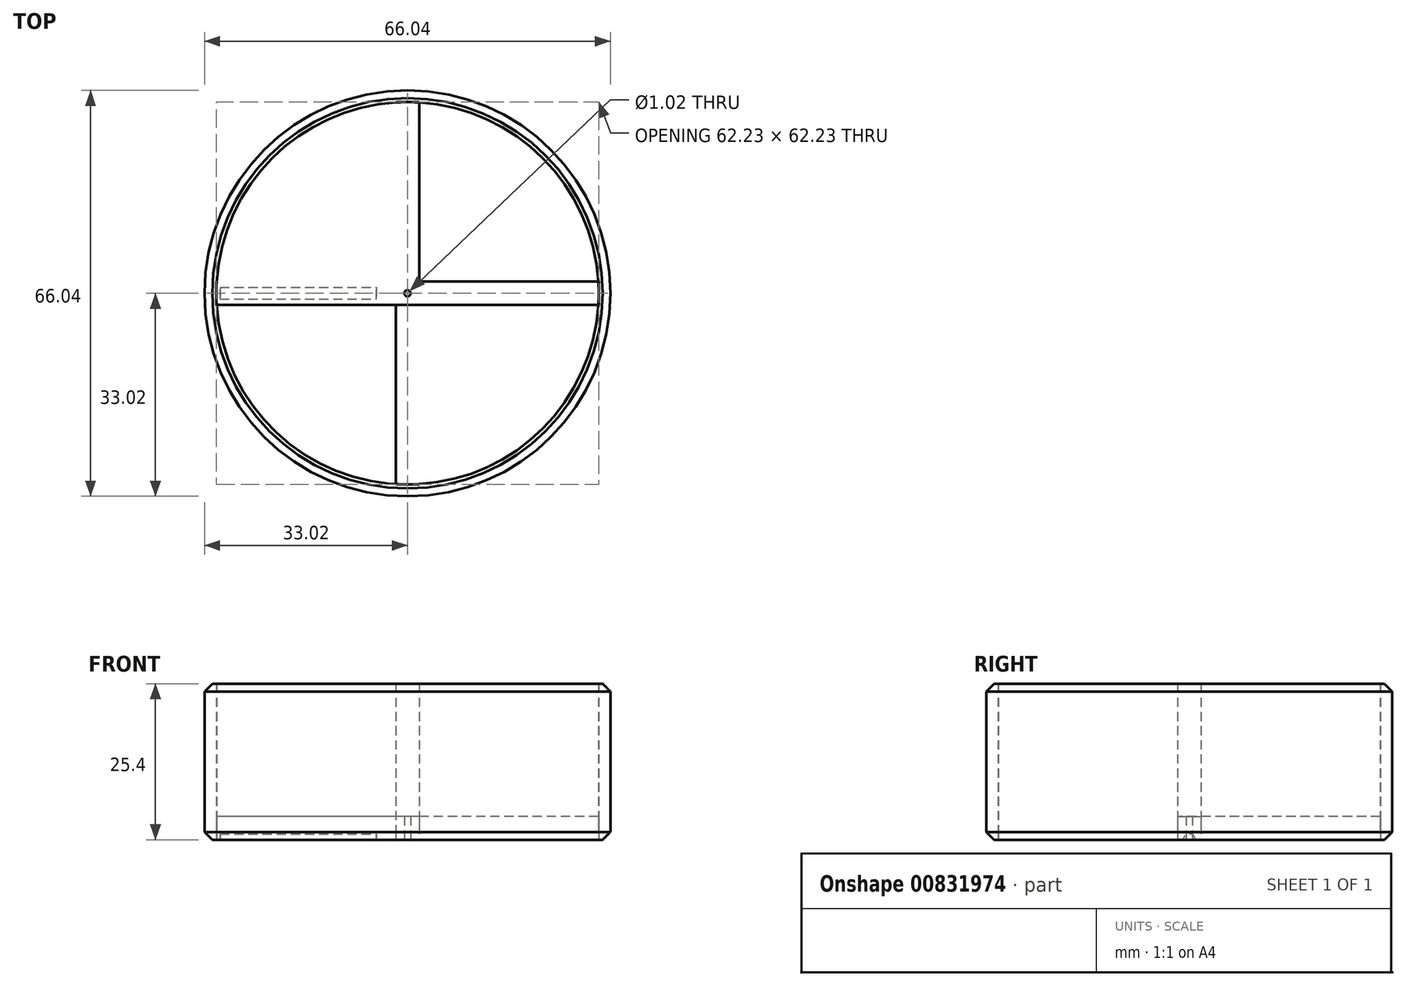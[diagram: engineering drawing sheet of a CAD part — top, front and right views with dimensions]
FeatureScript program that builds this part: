
annotation { "Feature Type Name" : "Feature", "Feature Type Description" : "" }
export const myFeature = defineFeature(function(context is Context, id is Id, definition is map)
    precondition{}
    {
        {
            var Q0;
            Q0=qCreatedBy(makeId("Top.planeOp"),FACE);
            var sketch = newSketch(context, id + "F0", { "sketchPlane" : qUnion([Q0])});
            skCircle(sketch, "E0", {"center": v(0, 0) * mm, "radius": 33.02 * mm});
            skCircle(sketch, "E1", {"center": v(0, 0) * mm, "radius": 31.12 * mm});
            skLineSegment(sketch, "E2.bottom", {"start": v(1.9, 31.12) * mm, "end": v(-1.9, 31.12) * mm});
            skLineSegment(sketch, "E2.top", {"start": v(1.9, -31.12) * mm, "end": v(-1.9, -31.12) * mm});
            skLineSegment(sketch, "E2.left", {"start": v(1.9, 31.12) * mm, "end": v(1.9, -31.12) * mm});
            skLineSegment(sketch, "E2.right", {"start": v(-1.9, 31.12) * mm, "end": v(-1.9, -31.06) * mm});
            skLineSegment(sketch, "E3.bottom", {"start": v(31.12, 1.9) * mm, "end": v(-31.12, 1.9) * mm});
            skLineSegment(sketch, "E3.top", {"start": v(31.12, -1.9) * mm, "end": v(-31.12, -1.9) * mm});
            skLineSegment(sketch, "E3.left", {"start": v(31.12, 1.9) * mm, "end": v(31.12, -1.9) * mm});
            skLineSegment(sketch, "E3.right", {"start": v(-31.12, 1.9) * mm, "end": v(-31.12, -1.9) * mm});
            skCircle(sketch, "E4", {"center": v(0, 0) * mm, "radius": 0.5 * mm});
            skSolve(sketch);
        }
        {
            var Q0;
            {var subQ0=sQuery(id+"F0.wireOp",EDGE,"E2.left");var subQ1=sQuery(id+"F0.wireOp",EDGE,"ze4YUoH1-U5XD-7e5n-4wEU-s4qru3D3CxTL");var subQ2=makeQuery(id+"F0.imprint","INTERSECT",VERTEX,{"disambiguationData":[OD(0.0)],"derivedFrom":[subQ1,subQ0]});Q0=makeQuery(id+"F0.imprint","IMPRINT",FACE,{"disambiguationData":[TD([[makeQuery(id+"F0.imprint","IMPRINT",EDGE,{"disambiguationData":[TD([[subQ2,-1.0]])],"derivedFrom":subQ1}),-1.0]])]});}
            var Q1;
            {var subQ0=sQuery(id+"F0.wireOp",EDGE,"E2.right");var subQ1=sQuery(id+"F0.wireOp",EDGE,"ze4YUoH1-U5XD-7e5n-4wEU-s4qru3D3CxTL");var subQ2=makeQuery(id+"F0.imprint","INTERSECT",VERTEX,{"disambiguationData":[OD(0.0)],"derivedFrom":[subQ1,subQ0]});Q1=makeQuery(id+"F0.imprint","IMPRINT",FACE,{"disambiguationData":[TD([[makeQuery(id+"F0.imprint","IMPRINT",EDGE,{"disambiguationData":[TD([[subQ2,-1.0]])],"derivedFrom":subQ1}),1.0]])]});}
            var Q2;
            {var subQ0=sQuery(id+"F0.wireOp",EDGE,"E2.left");var subQ1=sQuery(id+"F0.wireOp",EDGE,"ze4YUoH1-U5XD-7e5n-4wEU-s4qru3D3CxTL");var subQ2=makeQuery(id+"F0.imprint","INTERSECT",VERTEX,{"disambiguationData":[OD(0.0)],"derivedFrom":[subQ1,subQ0]});Q2=makeQuery(id+"F0.imprint","IMPRINT",FACE,{"disambiguationData":[TD([[makeQuery(id+"F0.imprint","IMPRINT",EDGE,{"disambiguationData":[TD([[subQ2,-1.0]])],"derivedFrom":subQ1}),1.0]])]});}
            var Q3;
            {var subQ0=sQuery(id+"F0.wireOp",EDGE,"E2.left");var subQ1=sQuery(id+"F0.wireOp",EDGE,"ze4YUoH1-U5XD-7e5n-4wEU-s4qru3D3CxTL");var subQ2=makeQuery(id+"F0.imprint","INTERSECT",VERTEX,{"disambiguationData":[OD(0.0)],"derivedFrom":[subQ1,subQ0]});Q3=makeQuery(id+"F0.imprint","IMPRINT",FACE,{"disambiguationData":[TD([[makeQuery(id+"F0.imprint","IMPRINT",EDGE,{"disambiguationData":[TD([[subQ2,1.0]])],"derivedFrom":subQ1}),1.0]])]});}
            var Q4;
            {var subQ0=sQuery(id+"F0.wireOp",EDGE,"E3.bottom");var subQ1=sQuery(id+"F0.wireOp",EDGE,"ze4YUoH1-U5XD-7e5n-4wEU-s4qru3D3CxTL");var subQ2=makeQuery(id+"F0.imprint","INTERSECT",VERTEX,{"disambiguationData":[OD(0.0)],"derivedFrom":[subQ1,subQ0]});Q4=makeQuery(id+"F0.imprint","IMPRINT",FACE,{"disambiguationData":[TD([[makeQuery(id+"F0.imprint","IMPRINT",EDGE,{"disambiguationData":[TD([[subQ2,1.0]])],"derivedFrom":subQ1}),1.0]])]});}
            var Q5;
            Q5=makeQuery(id+"F0.imprint","IMPRINT",FACE,{"disambiguationData":[TD([[makeQuery(id+"F0.imprint","IMPRINT",EDGE,{"derivedFrom":sQuery(id+"F0.wireOp",EDGE,"E4")}),-1.0]])]});
            var Q6;
            {var subQ0=sQuery(id+"F0.wireOp",EDGE,"E3.bottom");var subQ1=sQuery(id+"F0.wireOp",EDGE,"ze4YUoH1-U5XD-7e5n-4wEU-s4qru3D3CxTL");var subQ2=makeQuery(id+"F0.imprint","INTERSECT",VERTEX,{"disambiguationData":[OD(1.0)],"derivedFrom":[subQ1,subQ0]});Q6=makeQuery(id+"F0.imprint","IMPRINT",FACE,{"disambiguationData":[TD([[makeQuery(id+"F0.imprint","IMPRINT",EDGE,{"disambiguationData":[TD([[subQ2,-1.0]])],"derivedFrom":subQ1}),1.0]])]});}
            var Q7;
            {var subQ0=sQuery(id+"F0.wireOp",EDGE,"E3.top");var subQ1=sQuery(id+"F0.wireOp",EDGE,"ze4YUoH1-U5XD-7e5n-4wEU-s4qru3D3CxTL");var subQ2=makeQuery(id+"F0.imprint","INTERSECT",VERTEX,{"disambiguationData":[OD(0.0)],"derivedFrom":[subQ1,subQ0]});Q7=makeQuery(id+"F0.imprint","IMPRINT",FACE,{"disambiguationData":[TD([[makeQuery(id+"F0.imprint","IMPRINT",EDGE,{"disambiguationData":[TD([[subQ2,-1.0]])],"derivedFrom":subQ1}),1.0]])]});}
            var Q8;
            {var subQ0=sQuery(id+"F0.wireOp",EDGE,"E2.right");var subQ1=sQuery(id+"F0.wireOp",EDGE,"ze4YUoH1-U5XD-7e5n-4wEU-s4qru3D3CxTL");var subQ2=makeQuery(id+"F0.imprint","INTERSECT",VERTEX,{"disambiguationData":[OD(1.0)],"derivedFrom":[subQ1,subQ0]});Q8=makeQuery(id+"F0.imprint","IMPRINT",FACE,{"disambiguationData":[TD([[makeQuery(id+"F0.imprint","IMPRINT",EDGE,{"disambiguationData":[TD([[subQ2,-1.0]])],"derivedFrom":subQ1}),1.0]])]});}
            var Q9;
            {var subQ0=sQuery(id+"F0.wireOp",EDGE,"E2.left");var subQ1=sQuery(id+"F0.wireOp",EDGE,"ze4YUoH1-U5XD-7e5n-4wEU-s4qru3D3CxTL");var subQ2=makeQuery(id+"F0.imprint","INTERSECT",VERTEX,{"disambiguationData":[OD(1.0)],"derivedFrom":[subQ1,subQ0]});Q9=makeQuery(id+"F0.imprint","IMPRINT",FACE,{"disambiguationData":[TD([[makeQuery(id+"F0.imprint","IMPRINT",EDGE,{"disambiguationData":[TD([[subQ2,-1.0]])],"derivedFrom":subQ1}),1.0]])]});}
            var Q10;
            {var subQ0=sQuery(id+"F0.wireOp",EDGE,"E3.bottom");var subQ1=sQuery(id+"F0.wireOp",EDGE,"ze4YUoH1-U5XD-7e5n-4wEU-s4qru3D3CxTL");var subQ2=makeQuery(id+"F0.imprint","INTERSECT",VERTEX,{"disambiguationData":[OD(0.0)],"derivedFrom":[subQ1,subQ0]});Q10=makeQuery(id+"F0.imprint","IMPRINT",FACE,{"disambiguationData":[TD([[makeQuery(id+"F0.imprint","IMPRINT",EDGE,{"disambiguationData":[TD([[subQ2,1.0]])],"derivedFrom":subQ1}),-1.0]])]});}
            var Q11;
            {var subQ0=sQuery(id+"F0.wireOp",EDGE,"E2.right");var subQ1=sQuery(id+"F0.wireOp",EDGE,"ze4YUoH1-U5XD-7e5n-4wEU-s4qru3D3CxTL");var subQ2=makeQuery(id+"F0.imprint","INTERSECT",VERTEX,{"disambiguationData":[OD(1.0)],"derivedFrom":[subQ1,subQ0]});Q11=makeQuery(id+"F0.imprint","IMPRINT",FACE,{"disambiguationData":[TD([[makeQuery(id+"F0.imprint","IMPRINT",EDGE,{"disambiguationData":[TD([[subQ2,-1.0]])],"derivedFrom":subQ1}),-1.0]])]});}
            var Q12;
            {var subQ0=sQuery(id+"F0.wireOp",EDGE,"E3.bottom");var subQ1=sQuery(id+"F0.wireOp",EDGE,"ze4YUoH1-U5XD-7e5n-4wEU-s4qru3D3CxTL");var subQ2=makeQuery(id+"F0.imprint","INTERSECT",VERTEX,{"disambiguationData":[OD(1.0)],"derivedFrom":[subQ1,subQ0]});Q12=makeQuery(id+"F0.imprint","IMPRINT",FACE,{"disambiguationData":[TD([[makeQuery(id+"F0.imprint","IMPRINT",EDGE,{"disambiguationData":[TD([[subQ2,-1.0]])],"derivedFrom":subQ1}),-1.0]])]});}
            var Q13;
            {var subQ0=sQuery(id+"F0.wireOp",EDGE,"E3.bottom");var subQ1=sQuery(id+"F0.wireOp",EDGE,"E1");var subQ2=makeQuery(id+"F0.imprint","INTERSECT",VERTEX,{"disambiguationData":[OD(0.0)],"derivedFrom":[subQ1,subQ0]});Q13=makeQuery(id+"F0.imprint","IMPRINT",FACE,{"disambiguationData":[TD([[makeQuery(id+"F0.imprint","IMPRINT",EDGE,{"disambiguationData":[TD([[subQ2,1.0]])],"derivedFrom":subQ1}),1.0]])]});}
            var Q14;
            {var subQ0=sQuery(id+"F0.wireOp",EDGE,"E2.right");var subQ1=sQuery(id+"F0.wireOp",EDGE,"E1");var subQ2=makeQuery(id+"F0.imprint","INTERSECT",VERTEX,{"disambiguationData":[OD(0.0)],"derivedFrom":[subQ1,subQ0]});Q14=makeQuery(id+"F0.imprint","IMPRINT",FACE,{"disambiguationData":[TD([[makeQuery(id+"F0.imprint","IMPRINT",EDGE,{"disambiguationData":[TD([[subQ2,-1.0]])],"derivedFrom":subQ1}),1.0]])]});}
            var Q15;
            {var subQ0=sQuery(id+"F0.wireOp",EDGE,"E3.bottom");var subQ1=sQuery(id+"F0.wireOp",EDGE,"E1");var subQ2=makeQuery(id+"F0.imprint","INTERSECT",VERTEX,{"disambiguationData":[OD(1.0)],"derivedFrom":[subQ1,subQ0]});Q15=makeQuery(id+"F0.imprint","IMPRINT",FACE,{"disambiguationData":[TD([[makeQuery(id+"F0.imprint","IMPRINT",EDGE,{"disambiguationData":[TD([[subQ2,-1.0]])],"derivedFrom":subQ1}),1.0]])]});}
            var Q16;
            {var subQ1=sQuery(id+"F0.wireOp",EDGE,"E1");var subQ5=sQuery(id+"F0.wireOp",EDGE,"E2.left");var subQ6=makeQuery(id+"F0.imprint","INTERSECT",VERTEX,{"disambiguationData":[OD(0.0)],"derivedFrom":[subQ1,subQ5]});Q16=makeQuery(id+"F0.imprint","IMPRINT",FACE,{"disambiguationData":[TD([[makeQuery(id+"F0.imprint","IMPRINT",EDGE,{"disambiguationData":[TD([[subQ6,-1.0]])],"derivedFrom":subQ1}),1.0]])]});}
            extrude(context, id + "F1", {"entities" : qUnion([Q0, Q1, Q2, Q3, Q4, Q5, Q6, Q7, Q8, Q9, Q10, Q11, Q12, Q13, Q14, Q15, Q16]), "depth" : 3.8 * mm, "offsetDistance" : 25.4 * mm});
        }
        {
            var Q0;
            {var subQ0=sQuery(id+"F0.wireOp",EDGE,"E2.left");var subQ1=sQuery(id+"F0.wireOp",EDGE,"E1");var subQ2=makeQuery(id+"F0.imprint","INTERSECT",VERTEX,{"disambiguationData":[OD(0.0)],"derivedFrom":[subQ1,subQ0]});Q0=makeQuery(id+"F0.imprint","IMPRINT",FACE,{"disambiguationData":[TD([[makeQuery(id+"F0.imprint","IMPRINT",EDGE,{"disambiguationData":[TD([[subQ2,-1.0]])],"derivedFrom":subQ1}),1.0]])]});}
            var Q1;
            {var subQ0=sQuery(id+"F0.wireOp",EDGE,"E2.left");var subQ1=sQuery(id+"F0.wireOp",EDGE,"E1");var subQ2=makeQuery(id+"F0.imprint","INTERSECT",VERTEX,{"disambiguationData":[OD(1.0)],"derivedFrom":[subQ1,subQ0]});Q1=makeQuery(id+"F0.imprint","IMPRINT",FACE,{"disambiguationData":[TD([[makeQuery(id+"F0.imprint","IMPRINT",EDGE,{"disambiguationData":[TD([[subQ2,1.0]])],"derivedFrom":subQ1}),1.0]])]});}
            var Q2;
            {var subQ0=sQuery(id+"F0.wireOp",EDGE,"E2.right");var subQ1=sQuery(id+"F0.wireOp",EDGE,"E1");var subQ2=makeQuery(id+"F0.imprint","INTERSECT",VERTEX,{"disambiguationData":[OD(1.0)],"derivedFrom":[subQ1,subQ0]});Q2=makeQuery(id+"F0.imprint","IMPRINT",FACE,{"disambiguationData":[TD([[makeQuery(id+"F0.imprint","IMPRINT",EDGE,{"disambiguationData":[TD([[subQ2,-1.0]])],"derivedFrom":subQ1}),1.0]])]});}
            var Q3;
            {var subQ0=sQuery(id+"F0.wireOp",EDGE,"E2.right");var subQ1=sQuery(id+"F0.wireOp",EDGE,"E1");var subQ2=makeQuery(id+"F0.imprint","INTERSECT",VERTEX,{"disambiguationData":[OD(0.0)],"derivedFrom":[subQ1,subQ0]});Q3=makeQuery(id+"F0.imprint","IMPRINT",FACE,{"disambiguationData":[TD([[makeQuery(id+"F0.imprint","IMPRINT",EDGE,{"disambiguationData":[TD([[subQ2,1.0]])],"derivedFrom":subQ1}),1.0]])]});}
            var Q4;
            {var subQ0=sQuery(id+"F0.wireOp",EDGE,"E3.bottom");var subQ1=sQuery(id+"F0.wireOp",EDGE,"E1");var subQ2=makeQuery(id+"F0.imprint","INTERSECT",VERTEX,{"disambiguationData":[OD(0.0)],"derivedFrom":[subQ1,subQ0]});Q4=makeQuery(id+"F0.imprint","IMPRINT",FACE,{"disambiguationData":[TD([[makeQuery(id+"F0.imprint","IMPRINT",EDGE,{"disambiguationData":[TD([[subQ2,-1.0]])],"derivedFrom":subQ1}),1.0]])]});}
            var Q5;
            {var subQ0=sQuery(id+"F0.wireOp",EDGE,"E2.left");var subQ1=sQuery(id+"F0.wireOp",EDGE,"E1");var subQ2=makeQuery(id+"F0.imprint","INTERSECT",VERTEX,{"disambiguationData":[OD(1.0)],"derivedFrom":[subQ1,subQ0]});Q5=makeQuery(id+"F0.imprint","IMPRINT",FACE,{"disambiguationData":[TD([[makeQuery(id+"F0.imprint","IMPRINT",EDGE,{"disambiguationData":[TD([[subQ2,-1.0]])],"derivedFrom":subQ1}),1.0]])]});}
            extrude(context, id + "F2", {"entities" : qUnion([Q0, Q1, Q2, Q3, Q4, Q5]), "operationType" : NewBodyOperationType.ADD, "depth" : 1.27 * mm, "offsetDistance" : 25.4 * mm});
        }
        {
            var Q0;
            Q0=qCreatedBy(makeId("Right.planeOp"),FACE);
            cPlane(context, id + "F3", {"entities" : qUnion([Q0]), "cplaneType" : CPlaneType.OFFSET, "offset" : 5.08 * mm, "oppositeDirection" : true, "width" : 152.4 * mm, "height" : 152.4 * mm});
        }
        {
            var Q0;
            Q0=qCreatedBy(id+"F3.planeOp",FACE);
            var sketch = newSketch(context, id + "F4", { "sketchPlane" : qUnion([Q0])});
            skCircle(sketch, "E5", {"center": v(0, 0) * mm, "radius": 0.95 * mm});
            skSolve(sketch);
        }
        {
            var Q0;
            Q0 = qSketchRegion(id + "F4", true);
            extrude(context, id + "F5", {"entities" : qUnion([Q0]), "operationType" : NewBodyOperationType.REMOVE, "oppositeDirection" : true, "depth" : 25.4 * mm, "offsetDistance" : 25.4 * mm});
        }
        {
            var Q0;
            Q0=makeQuery(id+"F0.imprint","IMPRINT",FACE,{"disambiguationData":[TD([[makeQuery(id+"F0.imprint","IMPRINT",EDGE,{"derivedFrom":sQuery(id+"F0.wireOp",EDGE,"E0")}),1.0]])]});
            extrude(context, id + "F6", {"entities" : qUnion([Q0]), "depth" : 25.4 * mm, "offsetDistance" : 25.4 * mm});
        }
        {
            var Q0;
            Q0=makeQuery(id+"F6.opExtrude","CAP_EDGE",EDGE,{"disambiguationData":[OSD([sQuery(id+"F0.wireOp",EDGE,"E0")])],"isStart":false});
            var Q1;
            Q1=makeQuery(id+"F6.opExtrude","CAP_EDGE",EDGE,{"disambiguationData":[OSD([sQuery(id+"F0.wireOp",EDGE,"E0")])],"isStart":true});
            chamfer(context, id + "F7", {"entities" : qUnion([Q0, Q1]), "width" : 1.27 * mm, "tangentPropagation" : true});
        }
    });
